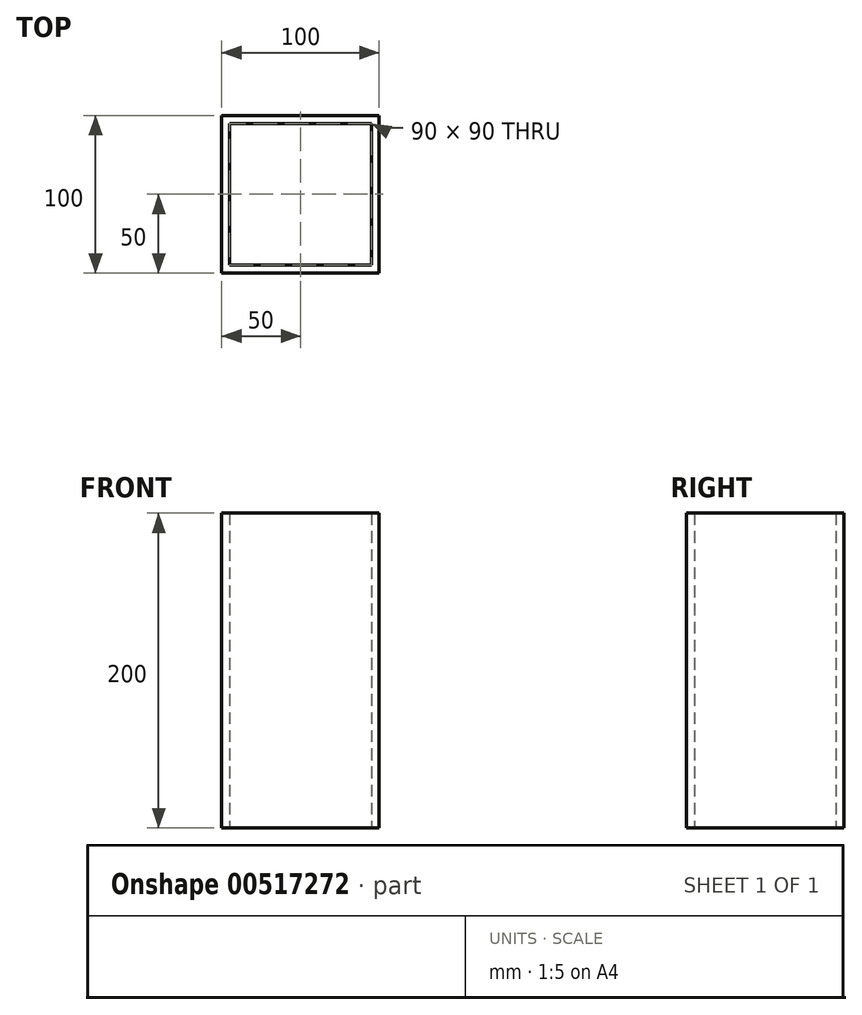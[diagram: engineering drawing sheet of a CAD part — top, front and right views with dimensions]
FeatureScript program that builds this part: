
annotation { "Feature Type Name" : "Feature", "Feature Type Description" : "" }
export const myFeature = defineFeature(function(context is Context, id is Id, definition is map)
    precondition{}
    {
        {
            var Q0;
            Q0=qCreatedBy(makeId("Top.planeOp"),FACE);
            var sketch = newSketch(context, id + "F0", { "sketchPlane" : qUnion([Q0])});
            skLineSegment(sketch, "E0.bottom", {"start": v(-50, 50) * mm, "end": v(50, 50) * mm});
            skLineSegment(sketch, "E0.top", {"start": v(-50, -50) * mm, "end": v(50, -50) * mm});
            skLineSegment(sketch, "E0.left", {"start": v(-50, 50) * mm, "end": v(-50, -50) * mm});
            skLineSegment(sketch, "E0.right", {"start": v(50, 50) * mm, "end": v(50, -50) * mm});
            skPoint(sketch, "E0.middle", {"position": v(0, 0) * mm});
            skLineSegment(sketch, "E1.bottom", {"start": v(-45, 45) * mm, "end": v(45, 45) * mm});
            skLineSegment(sketch, "E1.top", {"start": v(-45, -45) * mm, "end": v(45, -45) * mm});
            skLineSegment(sketch, "E1.left", {"start": v(-45, 45) * mm, "end": v(-45, -45) * mm});
            skLineSegment(sketch, "E1.right", {"start": v(45, 45) * mm, "end": v(45, -45) * mm});
            skSolve(sketch);
        }
        {
            var Q0;
            Q0=makeQuery(id+"F0.imprint","IMPRINT",FACE,{"disambiguationData":[TD([[makeQuery(id+"F0.imprint","IMPRINT",EDGE,{"derivedFrom":sQuery(id+"F0.wireOp",EDGE,"E0.bottom")}),-1.0]])]});
            extrude(context, id + "F1", {"entities" : qUnion([Q0]), "depth" : 200 * mm, "offsetDistance" : 25 * mm});
        }
    });
